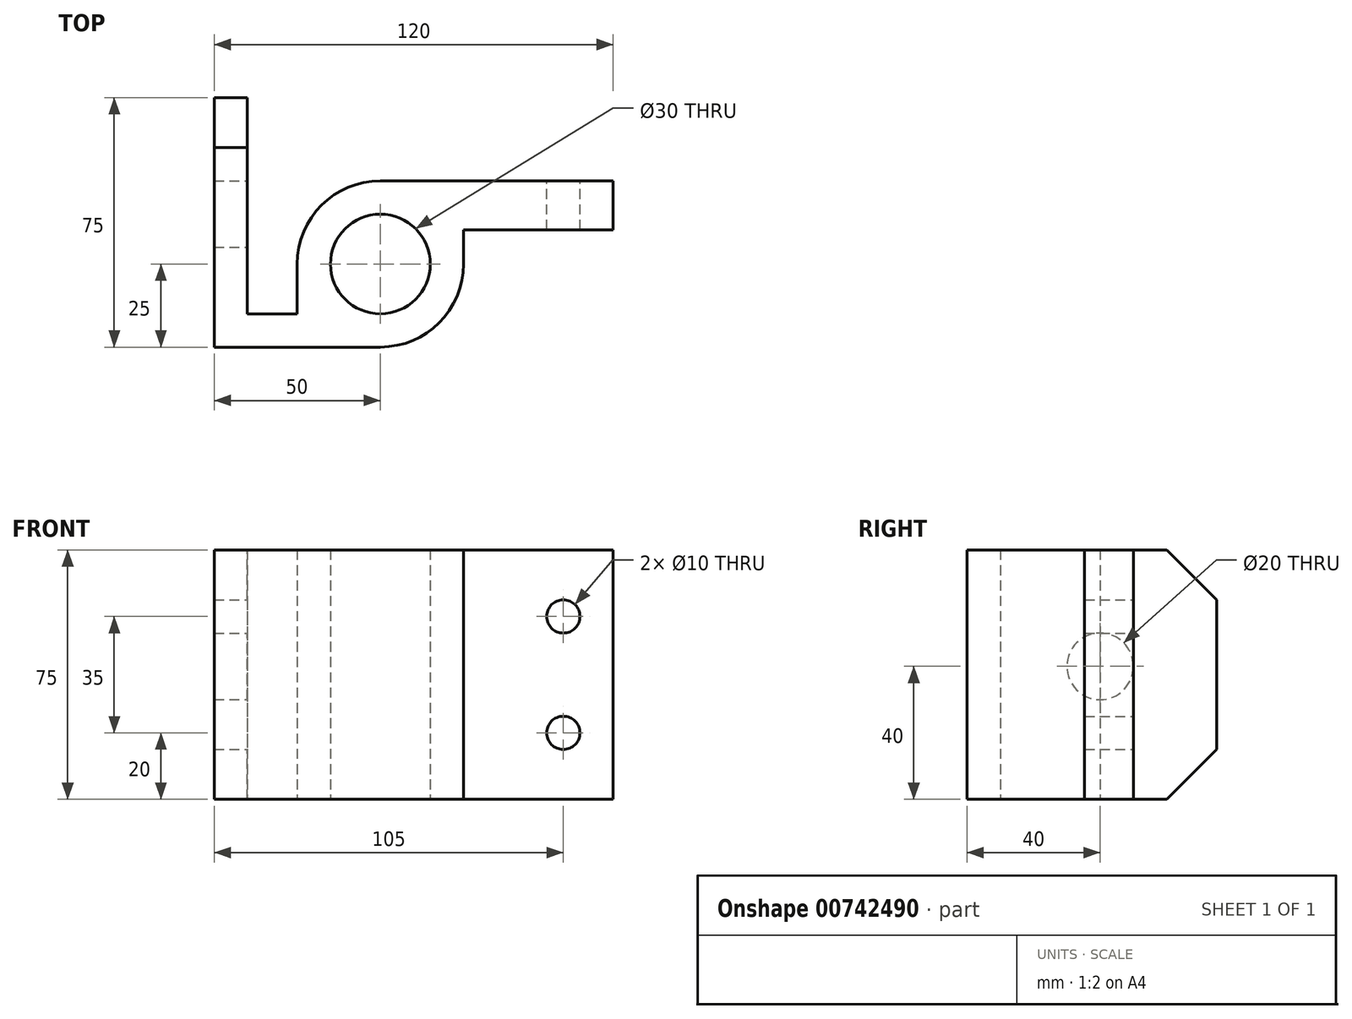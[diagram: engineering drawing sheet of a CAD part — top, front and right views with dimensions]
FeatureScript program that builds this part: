
annotation { "Feature Type Name" : "Feature", "Feature Type Description" : "" }
export const myFeature = defineFeature(function(context is Context, id is Id, definition is map)
    precondition{}
    {
        {
            var Q0;
            Q0=qCreatedBy(makeId("Top.planeOp"),FACE);
            var sketch = newSketch(context, id + "F0", { "sketchPlane" : qUnion([Q0])});
            skCircle(sketch, "E0", {"center": v(0, 0) * mm, "radius": 15 * mm});
            skArc(sketch, "E1", {"start": v(0, -25) * mm, "mid": v(17.68, -17.68) * mm, "end": v(25, 0) * mm});
            skLineSegment(sketch, "E2", {"start": v(0, -25) * mm, "end": v(-50, -25) * mm});
            skLineSegment(sketch, "E3", {"start": v(-50, -25) * mm, "end": v(-50, 50) * mm});
            skLineSegment(sketch, "E4", {"start": v(-25, -15) * mm, "end": v(-40, -15) * mm});
            skLineSegment(sketch, "E5", {"start": v(-25, 0) * mm, "end": v(-25, -15) * mm});
            skPoint(sketch, "E5.startSnap0", {"position": v(-25, -15) * mm});
            skLineSegment(sketch, "E6", {"start": v(-50, 50) * mm, "end": v(-40, 50) * mm});
            skLineSegment(sketch, "E7", {"start": v(-40, 50) * mm, "end": v(-40, -15) * mm});
            skPoint(sketch, "E8.orphan", {"position": v(-50, -15) * mm});
            skPoint(sketch, "E9.orphan", {"position": v(0, -15) * mm});
            skLineSegment(sketch, "E10", {"start": v(0, 25) * mm, "end": v(70, 25) * mm});
            skLineSegment(sketch, "E11", {"start": v(70, 25) * mm, "end": v(70, 10.3) * mm});
            skLineSegment(sketch, "E12", {"start": v(70, 10.3) * mm, "end": v(25, 10.3) * mm});
            skArc(sketch, "E13.trimOffspring", {"start": v(0, 25) * mm, "mid": v(-17.68, 17.68) * mm, "end": v(-25, 0) * mm});
            skLineSegment(sketch, "E14", {"start": v(25, 0) * mm, "end": v(25, 10.3) * mm});
            skSolve(sketch);
        }
        {
            var Q0;
            Q0=makeQuery(id+"F0.imprint","IMPRINT",FACE,{"disambiguationData":[TD([[makeQuery(id+"F0.imprint","IMPRINT",EDGE,{"derivedFrom":sQuery(id+"F0.wireOp",EDGE,"E0")}),-1.0]])]});
            extrude(context, id + "F1", {"entities" : qUnion([Q0]), "depth" : 75 * mm, "offsetDistance" : 25 * mm});
        }
        {
            var Q0;
            Q0=makeQuery(id+"F1.opExtrude","SWEPT_FACE",FACE,{"disambiguationData":[OSD([sQuery(id+"F0.wireOp",EDGE,"E10")])]});
            var sketch = newSketch(context, id + "F2", { "sketchPlane" : qUnion([Q0])});
            skLineSegment(sketch, "E15", {"start": v(-70, 0) * mm, "end": v(-55, 0) * mm});
            skPoint(sketch, "E16", {"position": v(-55, 20) * mm});
            skPoint(sketch, "E17", {"position": v(-55, 55) * mm});
            skCircle(sketch, "E18", {"center": v(-55, 20) * mm, "radius": 5 * mm});
            skCircle(sketch, "E19", {"center": v(-55, 55) * mm, "radius": 5 * mm});
            skPoint(sketch, "E20.orphan", {"position": v(-55, 75) * mm});
            skSolve(sketch);
        }
        {
            var Q0;
            Q0=makeQuery(id+"F2.imprint","IMPRINT",FACE,{"disambiguationData":[TD([[makeQuery(id+"F2.imprint","IMPRINT",EDGE,{"derivedFrom":sQuery(id+"F2.wireOp",EDGE,"E18")}),1.0]])]});
            var Q1;
            Q1=makeQuery(id+"F2.imprint","IMPRINT",FACE,{"disambiguationData":[TD([[makeQuery(id+"F2.imprint","IMPRINT",EDGE,{"derivedFrom":sQuery(id+"F2.wireOp",EDGE,"E19")}),1.0]])]});
            extrude(context, id + "F3", {"entities" : qUnion([Q0, Q1]), "operationType" : NewBodyOperationType.REMOVE, "oppositeDirection" : true, "depth" : 15 * mm, "offsetDistance" : 25 * mm});
        }
        {
            var Q0;
            Q0=makeQuery(id+"F1.opExtrude","SWEPT_FACE",FACE,{"disambiguationData":[OSD([sQuery(id+"F0.wireOp",EDGE,"E7")])]});
            var sketch = newSketch(context, id + "F4", { "sketchPlane" : qUnion([Q0])});
            skPoint(sketch, "E21", {"position": v(50, 75) * mm});
            skPoint(sketch, "E22", {"position": v(15, 75) * mm});
            skLineSegment(sketch, "E23", {"start": v(15, 75) * mm, "end": v(15, 40) * mm});
            skCircle(sketch, "E24", {"center": v(15, 40) * mm, "radius": 10 * mm});
            skSolve(sketch);
        }
        {
            var Q0;
            Q0=makeQuery(id+"F4.imprint","IMPRINT",FACE,{"disambiguationData":[TD([[makeQuery(id+"F4.imprint","IMPRINT",EDGE,{"derivedFrom":sQuery(id+"F4.wireOp",EDGE,"E24")}),1.0]])]});
            extrude(context, id + "F5", {"entities" : qUnion([Q0]), "operationType" : NewBodyOperationType.REMOVE, "oppositeDirection" : true, "depth" : 10 * mm, "offsetDistance" : 25 * mm});
        }
        {
            var Q0;
            Q0=makeQuery(id+"F1.opExtrude","SWEPT_FACE",FACE,{"disambiguationData":[OSD([sQuery(id+"F0.wireOp",EDGE,"E7")])]});
            var sketch = newSketch(context, id + "F6", { "sketchPlane" : qUnion([Q0])});
            skPoint(sketch, "E25", {"position": v(50, 75) * mm});
            skPoint(sketch, "E26", {"position": v(50, 60) * mm});
            skPoint(sketch, "E27", {"position": v(35, 75) * mm});
            skLineSegment(sketch, "E28", {"start": v(50, 60) * mm, "end": v(50, 75) * mm});
            skLineSegment(sketch, "E29", {"start": v(50, 75) * mm, "end": v(35, 75) * mm});
            skLineSegment(sketch, "E30", {"start": v(50, 60) * mm, "end": v(35, 75) * mm});
            skPoint(sketch, "E31", {"position": v(50, 0) * mm});
            skPoint(sketch, "E32", {"position": v(35, 0) * mm});
            skPoint(sketch, "E33", {"position": v(50, 15) * mm});
            skLineSegment(sketch, "E34", {"start": v(35, 0) * mm, "end": v(50, 15) * mm});
            skSolve(sketch);
        }
        {
            var Q0;
            Q0=makeQuery(id+"F6.imprint","IMPRINT",FACE,{"disambiguationData":[TD([[makeQuery(id+"F6.imprint","IMPRINT",EDGE,{"derivedFrom":sQuery(id+"F6.wireOp",EDGE,"E28")}),-1.0]])]});
            var Q1;
            {var subQ0=sQuery(id+"F6.wireOp",EDGE,"E34");Q1=makeQuery(id+"F6.imprint","IMPRINT",FACE,{"disambiguationData":[TD([[makeQuery(id+"F6.imprint","IMPRINT",EDGE,{"derivedFrom":subQ0}),-1.0]])]});}
            extrude(context, id + "F7", {"entities" : qUnion([Q0, Q1]), "operationType" : NewBodyOperationType.REMOVE, "oppositeDirection" : true, "depth" : 10 * mm, "offsetDistance" : 25 * mm});
        }
    });
